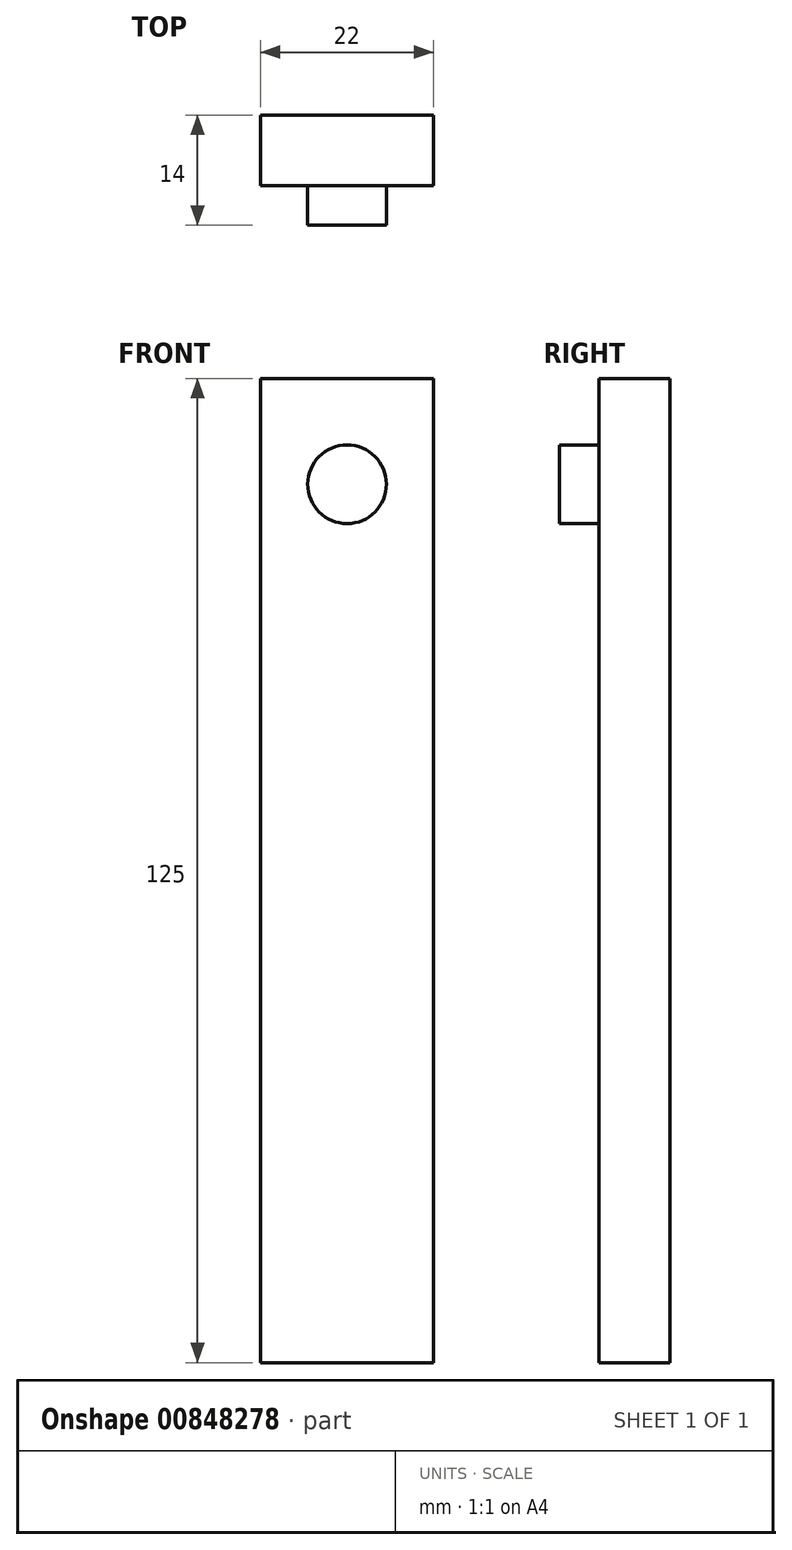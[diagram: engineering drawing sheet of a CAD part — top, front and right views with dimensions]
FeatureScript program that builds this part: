
annotation { "Feature Type Name" : "Feature", "Feature Type Description" : "" }
export const myFeature = defineFeature(function(context is Context, id is Id, definition is map)
    precondition{}
    {
        {
            var Q0;
            Q0=qCreatedBy(makeId("Top.planeOp"),FACE);
            var sketch = newSketch(context, id + "F0", { "sketchPlane" : qUnion([Q0])});
            skLineSegment(sketch, "E0.bottom", {"start": v(-11, 4.5) * mm, "end": v(11, 4.5) * mm});
            skLineSegment(sketch, "E0.top", {"start": v(-11, -4.5) * mm, "end": v(11, -4.5) * mm});
            skLineSegment(sketch, "E0.left", {"start": v(-11, 4.5) * mm, "end": v(-11, -4.5) * mm});
            skLineSegment(sketch, "E0.right", {"start": v(11, 4.5) * mm, "end": v(11, -4.5) * mm});
            skSolve(sketch);
        }
        {
            var Q0;
            Q0=makeQuery(id+"F0.imprint","IMPRINT",FACE,{"disambiguationData":[TD([[makeQuery(id+"F0.imprint","IMPRINT",EDGE,{"derivedFrom":sQuery(id+"F0.wireOp",EDGE,"E0.bottom")}),-1.0]])]});
            var sketch = newSketch(context, id + "F1", { "sketchPlane" : qUnion([Q0])});
            skSolve(sketch);
        }
        {
            var Q0;
            Q0=makeQuery(id+"F1.imprint","IMPRINT",FACE,{"disambiguationData":[TD([[makeQuery(id+"F1.imprint","IMPRINT",EDGE,{"derivedFrom":makeQuery(id+"F0.imprint","IMPRINT",EDGE,{"derivedFrom":sQuery(id+"F0.wireOp",EDGE,"E0.bottom")})}),-1.0]])]});
            extrude(context, id + "F2", {"entities" : qUnion([Q0]), "depth" : 25 * mm, "offsetDistance" : 25 * mm});
        }
        {
            var Q0;
            Q0=makeQuery(id+"F2.opExtrude","CAP_FACE",FACE,{"disambiguationData":[OSD([sQuery(id+"F0.wireOp",EDGE,"E0.bottom"),sQuery(id+"F0.wireOp",EDGE,"E0.top"),sQuery(id+"F0.wireOp",EDGE,"E0.left"),sQuery(id+"F0.wireOp",EDGE,"E0.right")])],"isStart":false});
            extrude(context, id + "F3", {"entities" : qUnion([Q0]), "operationType" : NewBodyOperationType.ADD, "depth" : 100 * mm, "offsetDistance" : 25 * mm});
        }
        {
            var Q0;
            {var subQ0=sQuery(id+"F0.wireOp",EDGE,"E0.top");Q0=makeQuery(id+"F3.boolean.opBoolean","MERGE",FACE,{"derivedFrom":[makeQuery(id+"F2.opExtrude","SWEPT_FACE",FACE,{"disambiguationData":[OSD([subQ0])]}),makeQuery(id+"F3.opExtrude","SWEPT_FACE",FACE,{"disambiguationData":[OSD([subQ0])]})]});}
            var sketch = newSketch(context, id + "F4", { "sketchPlane" : qUnion([Q0])});
            skCircle(sketch, "E1", {"center": v(0, 111.58) * mm, "radius": 5 * mm});
            skSolve(sketch);
        }
        {
            var Q0;
            Q0=makeQuery(id+"F4.imprint","IMPRINT",FACE,{"disambiguationData":[TD([[makeQuery(id+"F4.imprint","IMPRINT",EDGE,{"derivedFrom":sQuery(id+"F4.wireOp",EDGE,"E1")}),1.0]])]});
            extrude(context, id + "F5", {"entities" : qUnion([Q0]), "operationType" : NewBodyOperationType.ADD, "depth" : 5 * mm, "offsetDistance" : 25 * mm});
        }
    });
